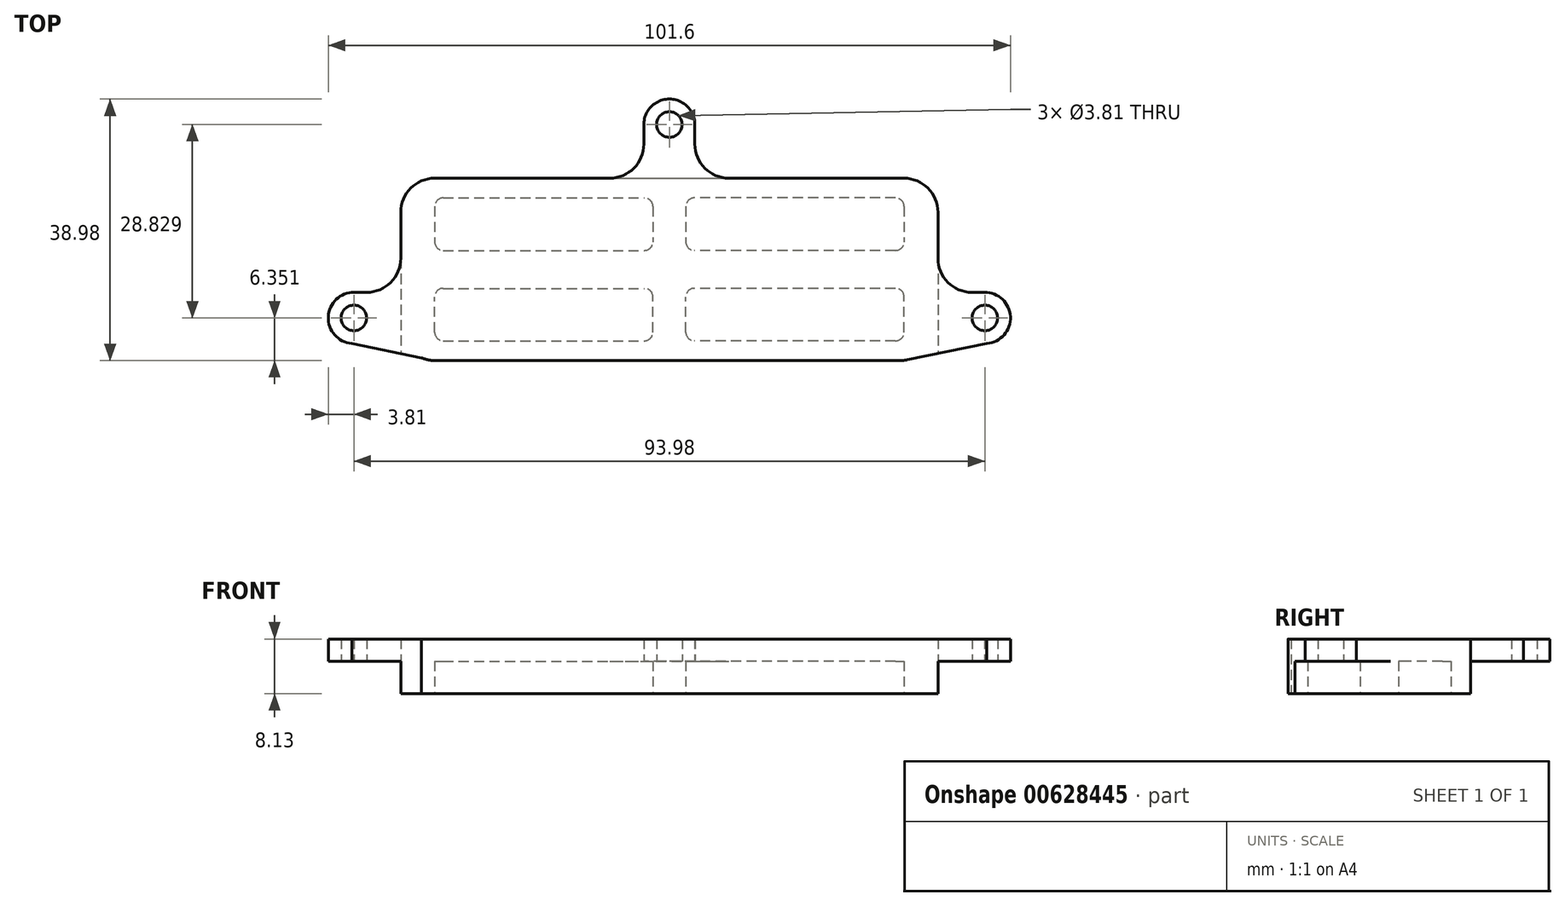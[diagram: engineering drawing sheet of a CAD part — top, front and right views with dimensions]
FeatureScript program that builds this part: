
annotation { "Feature Type Name" : "Feature", "Feature Type Description" : "" }
export const myFeature = defineFeature(function(context is Context, id is Id, definition is map)
    precondition{}
    {
        {
            var Q0;
            Q0=qCreatedBy(makeId("Top.planeOp"),FACE);
            var sketch = newSketch(context, id + "F0", { "sketchPlane" : qUnion([Q0])});
            skLineSegment(sketch, "E0.bottom", {"start": v(-34.93, 13.59) * mm, "end": v(-8.88, 13.59) * mm});
            skLineSegment(sketch, "E0.top", {"start": v(-34.93, -13.59) * mm, "end": v(34.4, -13.59) * mm});
            skLineSegment(sketch, "E0.left", {"start": v(-40, 8.5) * mm, "end": v(-40, 1.65) * mm});
            skLineSegment(sketch, "E0.right", {"start": v(40, 8.5) * mm, "end": v(40, 1.65) * mm});
            skPoint(sketch, "E0.middle", {"position": v(0, 0) * mm});
            skPoint(sketch, "E1", {"position": v(-47, -7.24) * mm});
            skPoint(sketch, "E2.MirrorP", {"position": v(47, -7.24) * mm});
            skPoint(sketch, "E3", {"position": v(0, 21.59) * mm});
            skPoint(sketch, "E4", {"position": v(-9.31, -13.59) * mm});
            skPoint(sketch, "E5.visualSharp", {"position": v(-40, 13.59) * mm});
            skArc(sketch, "E5.filletArc", {"start": v(-34.93, 13.59) * mm, "mid": v(-38.52, 12.1) * mm, "end": v(-40, 8.5) * mm});
            skArc(sketch, "E6.MirrorCS", {"start": v(-34.93, -13.59) * mm, "mid": v(-35.95, -13.48) * mm, "end": v(-36.94, -13.17) * mm});
            skArc(sketch, "E7.MirrorCS", {"start": v(34.93, 13.59) * mm, "mid": v(38.52, 12.1) * mm, "end": v(40, 8.5) * mm});
            skCircle(sketch, "E8", {"center": v(47, -7.24) * mm, "radius": 3.81 * mm});
            skCircle(sketch, "E9", {"center": v(-47, -7.24) * mm, "radius": 3.81 * mm});
            skCircle(sketch, "E10", {"center": v(0, 21.59) * mm, "radius": 3.8 * mm});
            skPoint(sketch, "E11.orphan", {"position": v(40, 13.59) * mm});
            skPoint(sketch, "E12.orphan", {"position": v(40, -13.59) * mm});
            skLineSegment(sketch, "E13", {"start": v(-3.8, 21.72) * mm, "end": v(-3.8, 18.67) * mm});
            skArc(sketch, "E14.filletArc", {"start": v(-8.88, 13.59) * mm, "mid": v(-5.29, 15.08) * mm, "end": v(-3.8, 18.67) * mm});
            skArc(sketch, "E15.MirrorCS", {"start": v(8.88, 13.59) * mm, "mid": v(5.29, 15.08) * mm, "end": v(3.8, 18.67) * mm});
            skLineSegment(sketch, "E16.MirrorCS", {"start": v(3.8, 21.72) * mm, "end": v(3.8, 18.67) * mm});
            skLineSegment(sketch, "E17", {"start": v(-47.04, -3.43) * mm, "end": v(-45.09, -3.43) * mm});
            skPoint(sketch, "E17.endSnap0", {"position": v(-40, -2.54) * mm});
            skPoint(sketch, "E18.newPointA", {"position": v(-40, -3.43) * mm});
            skPoint(sketch, "E18.newPointB", {"position": v(-40, -13.59) * mm});
            skArc(sketch, "E18.filletArc", {"start": v(-45.09, -3.43) * mm, "mid": v(-41.5, -1.94) * mm, "end": v(-40, 1.65) * mm});
            skArc(sketch, "E19.MirrorCS", {"start": v(45.09, -3.43) * mm, "mid": v(41.5, -1.94) * mm, "end": v(40, 1.65) * mm});
            skLineSegment(sketch, "E20.MirrorCS", {"start": v(47.04, -3.43) * mm, "end": v(45.09, -3.43) * mm});
            skLineSegment(sketch, "E21", {"start": v(47.3, -11.04) * mm, "end": v(35.43, -13.48) * mm});
            skPoint(sketch, "E22.orphan", {"position": v(40, -8.5) * mm});
            skPoint(sketch, "E23.visualSharp", {"position": v(34.93, -13.59) * mm});
            skArc(sketch, "E23.filletArc", {"start": v(34.4, -13.59) * mm, "mid": v(34.92, -13.56) * mm, "end": v(35.43, -13.48) * mm});
            skLineSegment(sketch, "E24.MirrorCS", {"start": v(-47.3, -11.04) * mm, "end": v(-35.43, -13.48) * mm});
            skPoint(sketch, "E25.orphan", {"position": v(-40, -8.5) * mm});
            skCircle(sketch, "E26", {"center": v(0, 21.59) * mm, "radius": 1.9 * mm});
            skCircle(sketch, "E27", {"center": v(-47, -7.24) * mm, "radius": 1.9 * mm});
            skCircle(sketch, "E28", {"center": v(47, -7.24) * mm, "radius": 1.9 * mm});
            skPoint(sketch, "E29.visualSharp", {"position": v(-34.16, 7.75) * mm});
            skPoint(sketch, "E30.orphan", {"position": v(-34.16, -7.75) * mm});
            skPoint(sketch, "E31.orphan", {"position": v(34.16, -7.75) * mm});
            skPoint(sketch, "E32.orphan", {"position": v(34.16, 7.75) * mm});
            skLineSegment(sketch, "E33", {"start": v(8.88, 13.59) * mm, "end": v(34.93, 13.59) * mm});
            skPoint(sketch, "E29.filletArc.end.orphan", {"position": v(-34.16, 5.2) * mm});
            skPoint(sketch, "E29.filletArc.start.orphan", {"position": v(-31.62, 7.75) * mm});
            skPoint(sketch, "E34.MirrorCS.end.orphan", {"position": v(-34.16, -5.2) * mm});
            skPoint(sketch, "E35.top.start.orphan", {"position": v(-31.62, -7.75) * mm});
            skPoint(sketch, "E36.MirrorCS.start.orphan", {"position": v(31.62, -7.75) * mm});
            skPoint(sketch, "E35.right.end.orphan", {"position": v(34.16, -5.2) * mm});
            skPoint(sketch, "E37.MirrorCS.end.orphan", {"position": v(34.16, 5.2) * mm});
            skPoint(sketch, "E37.MirrorCS.start.orphan", {"position": v(31.62, 7.75) * mm});
            skLineSegment(sketch, "E38", {"start": v(-40, 1.65) * mm, "end": v(-40, -12.54) * mm});
            skSolve(sketch);
        }
        {
            var Q0;
            Q0=qSketchRegion(id+"F0",true);
            extrude(context, id + "F1", {"entities" : qUnion([Q0]), "depth" : 3.3 * mm, "offsetDistance" : 25.4 * mm});
        }
        {
            var Q0;
            Q0=makeQuery(id+"F1.opExtrude","CAP_FACE",FACE,{"disambiguationData":[OSD([sQuery(id+"F0.wireOp",EDGE,"E0.bottom"),sQuery(id+"F0.wireOp",EDGE,"E0.top"),sQuery(id+"F0.wireOp",EDGE,"E0.left"),sQuery(id+"F0.wireOp",EDGE,"E0.right"),sQuery(id+"F0.wireOp",EDGE,"E5.filletArc"),sQuery(id+"F0.wireOp",EDGE,"E6.MirrorCS"),sQuery(id+"F0.wireOp",EDGE,"E7.MirrorCS"),sQuery(id+"F0.wireOp",EDGE,"E8"),sQuery(id+"F0.wireOp",EDGE,"E9"),sQuery(id+"F0.wireOp",EDGE,"E10"),sQuery(id+"F0.wireOp",EDGE,"E13"),sQuery(id+"F0.wireOp",EDGE,"E14.filletArc"),sQuery(id+"F0.wireOp",EDGE,"E15.MirrorCS"),sQuery(id+"F0.wireOp",EDGE,"E16.MirrorCS"),sQuery(id+"F0.wireOp",EDGE,"E17"),sQuery(id+"F0.wireOp",EDGE,"E18.filletArc"),sQuery(id+"F0.wireOp",EDGE,"E19.MirrorCS"),sQuery(id+"F0.wireOp",EDGE,"E20.MirrorCS"),sQuery(id+"F0.wireOp",EDGE,"E21"),sQuery(id+"F0.wireOp",EDGE,"E23.filletArc"),sQuery(id+"F0.wireOp",EDGE,"E24.MirrorCS"),sQuery(id+"F0.wireOp",EDGE,"E26"),sQuery(id+"F0.wireOp",EDGE,"E27"),sQuery(id+"F0.wireOp",EDGE,"E28"),sQuery(id+"F0.wireOp",EDGE,"E33")])],"isStart":true});
            var sketch = newSketch(context, id + "F2", { "sketchPlane" : qUnion([Q0])});
            skLineSegment(sketch, "E39", {"start": v(-40, -5.08) * mm, "end": v(-40, 12.54) * mm});
            skLineSegment(sketch, "E40.MirrorCS", {"start": v(40, -5.08) * mm, "end": v(40, 12.54) * mm});
            skLineSegment(sketch, "E41", {"start": v(-13.13, -13.59) * mm, "end": v(9.64, -13.59) * mm});
            skSolve(sketch);
        }
        {
            var Q0;
            Q0=qSketchRegion(id+"F2",true);
            var Q1;
            Q1=makeQuery(id+"F2.imprint","IMPRINT",FACE,{"disambiguationData":[TD([[makeQuery(id+"F2.imprint","IMPRINT",EDGE,{"derivedFrom":makeQuery(id+"F1.opExtrude","CAP_EDGE",EDGE,{"disambiguationData":[OSD([sQuery(id+"F0.wireOp",EDGE,"E0.top")])],"isStart":true})}),-1.0]])]});
            extrude(context, id + "F3", {"entities" : qUnion([Q0, Q1]), "operationType" : NewBodyOperationType.ADD, "depth" : 4.83 * mm, "offsetDistance" : 25.4 * mm});
        }
        {
            var Q0;
            Q0=makeQuery(id+"F3.opExtrude","CAP_FACE",FACE,{"disambiguationData":[OSD([sQuery(id+"F0.wireOp",EDGE,"E0.bottom"),sQuery(id+"F0.wireOp",EDGE,"E0.top"),sQuery(id+"F0.wireOp",EDGE,"E0.right"),sQuery(id+"F0.wireOp",EDGE,"E5.filletArc"),sQuery(id+"F0.wireOp",EDGE,"E6.MirrorCS"),sQuery(id+"F0.wireOp",EDGE,"E7.MirrorCS"),sQuery(id+"F0.wireOp",EDGE,"E21"),sQuery(id+"F0.wireOp",EDGE,"E23.filletArc"),sQuery(id+"F0.wireOp",EDGE,"E24.MirrorCS"),sQuery(id+"F2.wireOp",EDGE,"E39"),sQuery(id+"F2.wireOp",EDGE,"E40.MirrorCS"),sQuery(id+"F2.wireOp",EDGE,"E41")])],"isStart":false});
            var sketch = newSketch(context, id + "F4", { "sketchPlane" : qUnion([Q0])});
            skLineSegment(sketch, "E42.MirrorCS", {"start": v(-33.69, -2.83) * mm, "end": v(-3.72, -2.83) * mm});
            skLineSegment(sketch, "E43.MirrorCS", {"start": v(-2.45, -9.38) * mm, "end": v(-2.45, -4.1) * mm});
            skLineSegment(sketch, "E44.MirrorCS", {"start": v(-33.69, -10.65) * mm, "end": v(-3.72, -10.65) * mm});
            skLineSegment(sketch, "E45.MirrorCS", {"start": v(-34.96, -9.38) * mm, "end": v(-34.96, -4.1) * mm});
            skPoint(sketch, "E46.visualSharp", {"position": v(-34.96, -2.83) * mm});
            skArc(sketch, "E46.filletArc", {"start": v(-33.69, -2.83) * mm, "mid": v(-34.58, -3.2) * mm, "end": v(-34.96, -4.1) * mm});
            skPoint(sketch, "E47.visualSharp", {"position": v(-2.45, -2.83) * mm});
            skArc(sketch, "E47.filletArc", {"start": v(-2.45, -4.1) * mm, "mid": v(-2.82, -3.2) * mm, "end": v(-3.72, -2.83) * mm});
            skPoint(sketch, "E48.visualSharp", {"position": v(-2.45, -10.65) * mm});
            skArc(sketch, "E48.filletArc", {"start": v(-3.72, -10.65) * mm, "mid": v(-2.82, -10.27) * mm, "end": v(-2.45, -9.38) * mm});
            skPoint(sketch, "E49.visualSharp", {"position": v(-34.96, -10.65) * mm});
            skArc(sketch, "E49.filletArc", {"start": v(-34.96, -9.38) * mm, "mid": v(-34.58, -10.27) * mm, "end": v(-33.69, -10.65) * mm});
            skLineSegment(sketch, "E50.MirrorCS", {"start": v(2.45, -9.38) * mm, "end": v(2.45, -4.1) * mm});
            skArc(sketch, "E51.MirrorCS", {"start": v(2.45, -4.1) * mm, "mid": v(2.82, -3.2) * mm, "end": v(3.72, -2.83) * mm});
            skArc(sketch, "E52.MirrorCS", {"start": v(3.72, -10.65) * mm, "mid": v(2.82, -10.27) * mm, "end": v(2.45, -9.38) * mm});
            skLineSegment(sketch, "E53.MirrorCS", {"start": v(33.69, -10.65) * mm, "end": v(3.72, -10.65) * mm});
            skArc(sketch, "E54.MirrorCS", {"start": v(34.96, -9.38) * mm, "mid": v(34.58, -10.27) * mm, "end": v(33.69, -10.65) * mm});
            skLineSegment(sketch, "E55.MirrorCS", {"start": v(34.96, -9.38) * mm, "end": v(34.96, -4.1) * mm});
            skArc(sketch, "E56.MirrorCS", {"start": v(33.69, -2.83) * mm, "mid": v(34.58, -3.2) * mm, "end": v(34.96, -4.1) * mm});
            skLineSegment(sketch, "E57.MirrorCS", {"start": v(33.69, -2.83) * mm, "end": v(3.72, -2.83) * mm});
            skLineSegment(sketch, "E58.MirrorCS", {"start": v(-33.69, 2.83) * mm, "end": v(-3.72, 2.83) * mm});
            skArc(sketch, "E59.MirrorCS", {"start": v(-2.45, 4.1) * mm, "mid": v(-2.82, 3.2) * mm, "end": v(-3.72, 2.83) * mm});
            skLineSegment(sketch, "E60.MirrorCS", {"start": v(-2.45, 9.38) * mm, "end": v(-2.45, 4.1) * mm});
            skArc(sketch, "E61.MirrorCS", {"start": v(-3.72, 10.65) * mm, "mid": v(-2.82, 10.27) * mm, "end": v(-2.45, 9.38) * mm});
            skLineSegment(sketch, "E62.MirrorCS", {"start": v(-33.69, 10.65) * mm, "end": v(-3.72, 10.65) * mm});
            skArc(sketch, "E63.MirrorCS", {"start": v(-34.96, 9.38) * mm, "mid": v(-34.58, 10.27) * mm, "end": v(-33.69, 10.65) * mm});
            skLineSegment(sketch, "E64.MirrorCS", {"start": v(-34.96, 9.38) * mm, "end": v(-34.96, 4.1) * mm});
            skArc(sketch, "E65.MirrorCS", {"start": v(-33.69, 2.83) * mm, "mid": v(-34.58, 3.2) * mm, "end": v(-34.96, 4.1) * mm});
            skLineSegment(sketch, "E66.MirrorCS", {"start": v(2.45, 9.38) * mm, "end": v(2.45, 4.1) * mm});
            skArc(sketch, "E67.MirrorCS", {"start": v(3.72, 10.65) * mm, "mid": v(2.82, 10.27) * mm, "end": v(2.45, 9.38) * mm});
            skLineSegment(sketch, "E68.MirrorCS", {"start": v(33.69, 10.65) * mm, "end": v(3.72, 10.65) * mm});
            skArc(sketch, "E69.MirrorCS", {"start": v(34.96, 9.38) * mm, "mid": v(34.58, 10.27) * mm, "end": v(33.69, 10.65) * mm});
            skLineSegment(sketch, "E70.MirrorCS", {"start": v(34.96, 9.38) * mm, "end": v(34.96, 4.1) * mm});
            skArc(sketch, "E71.MirrorCS", {"start": v(33.69, 2.83) * mm, "mid": v(34.58, 3.2) * mm, "end": v(34.96, 4.1) * mm});
            skLineSegment(sketch, "E72.MirrorCS", {"start": v(33.69, 2.83) * mm, "end": v(3.72, 2.83) * mm});
            skArc(sketch, "E73.MirrorCS", {"start": v(2.45, 4.1) * mm, "mid": v(2.82, 3.2) * mm, "end": v(3.72, 2.83) * mm});
            skSolve(sketch);
        }
        {
            var Q0;
            Q0=makeQuery(id+"F4.imprint","IMPRINT",FACE,{"disambiguationData":[TD([[makeQuery(id+"F4.imprint","IMPRINT",EDGE,{"derivedFrom":sQuery(id+"F4.wireOp",EDGE,"E58.MirrorCS")}),1.0]])]});
            var Q1;
            Q1=makeQuery(id+"F4.imprint","IMPRINT",FACE,{"disambiguationData":[TD([[makeQuery(id+"F4.imprint","IMPRINT",EDGE,{"derivedFrom":sQuery(id+"F4.wireOp",EDGE,"E66.MirrorCS")}),1.0]])]});
            var Q2;
            Q2=makeQuery(id+"F4.imprint","IMPRINT",FACE,{"disambiguationData":[TD([[makeQuery(id+"F4.imprint","IMPRINT",EDGE,{"derivedFrom":sQuery(id+"F4.wireOp",EDGE,"E42.MirrorCS")}),-1.0]])]});
            var Q3;
            Q3=makeQuery(id+"F4.imprint","IMPRINT",FACE,{"disambiguationData":[TD([[makeQuery(id+"F4.imprint","IMPRINT",EDGE,{"derivedFrom":sQuery(id+"F4.wireOp",EDGE,"E50.MirrorCS")}),-1.0]])]});
            var Q4;
            Q4 = qSketchRegion(id + "F7", true);
            extrude(context, id + "F5", {"entities" : qUnion([Q0, Q1, Q2, Q3, Q4]), "operationType" : NewBodyOperationType.REMOVE, "oppositeDirection" : true, "depth" : 4.83 * mm, "offsetDistance" : 25.4 * mm});
        }
    });
